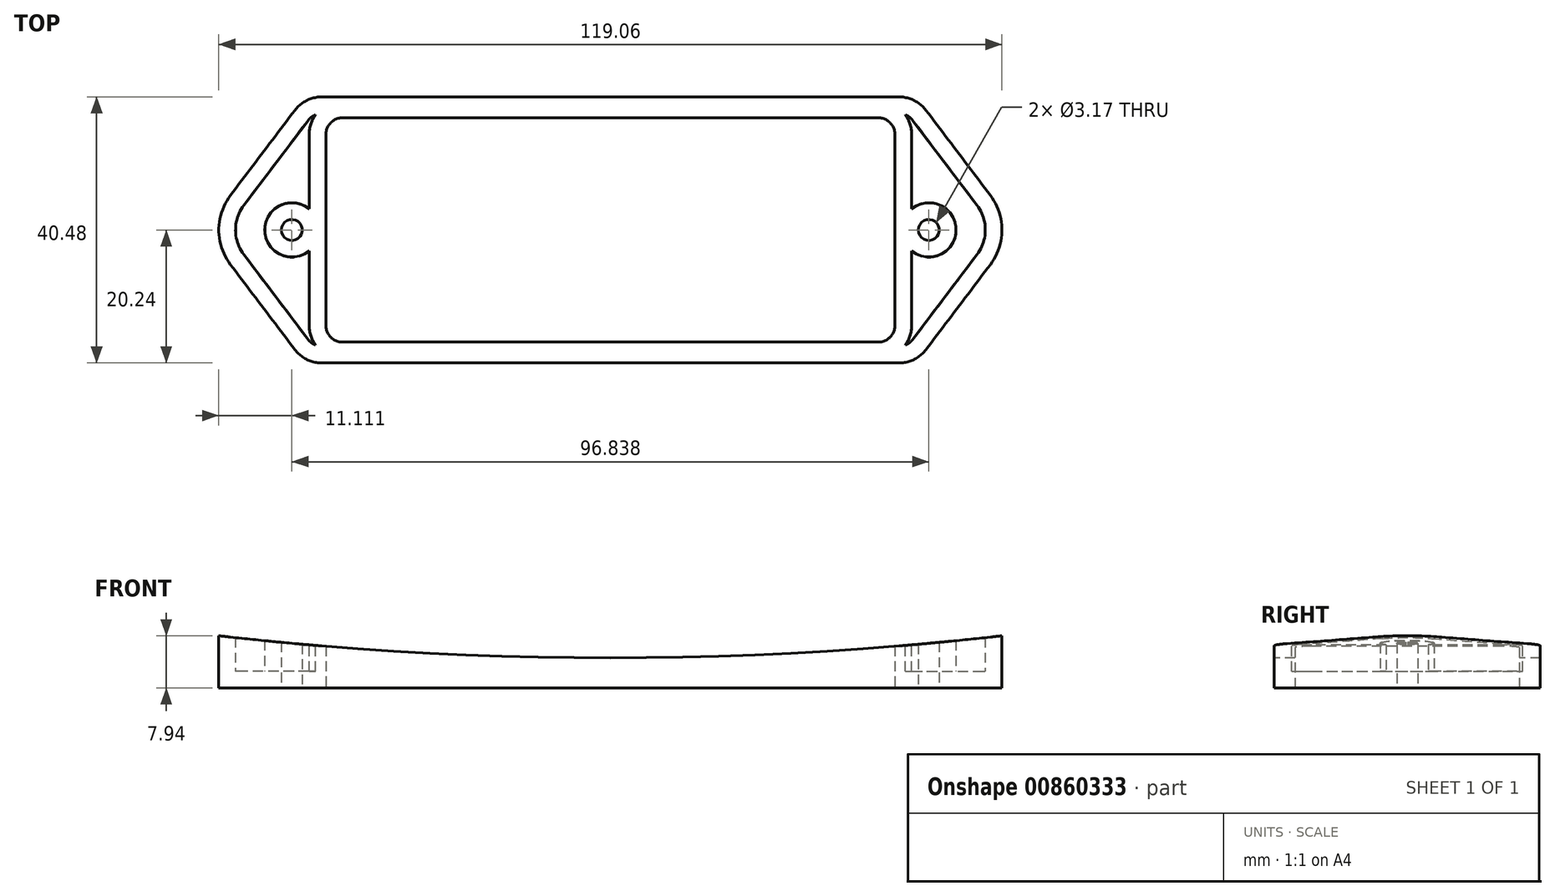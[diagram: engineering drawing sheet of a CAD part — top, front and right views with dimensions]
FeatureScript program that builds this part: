
annotation { "Feature Type Name" : "Feature", "Feature Type Description" : "" }
export const myFeature = defineFeature(function(context is Context, id is Id, definition is map)
    precondition{}
    {
        {
            var Q0;
            Q0=qCreatedBy(makeId("Top.planeOp"),FACE);
            var sketch = newSketch(context, id + "F0", { "sketchPlane" : qUnion([Q0])});
            skLineSegment(sketch, "E0.bottom", {"start": v(43.26, -17.07) * mm, "end": v(-43.26, -17.07) * mm});
            skLineSegment(sketch, "E0.top", {"start": v(43.26, 17.07) * mm, "end": v(-43.26, 17.07) * mm});
            skLineSegment(sketch, "E0.left", {"start": v(43.26, -17.07) * mm, "end": v(43.26, 17.07) * mm});
            skLineSegment(sketch, "E0.right", {"start": v(-43.26, -17.07) * mm, "end": v(-43.26, 17.07) * mm});
            skPoint(sketch, "E0.middle", {"position": v(0, 0) * mm});
            skLineSegment(sketch, "E1.bottom", {"start": v(46.43, -20.24) * mm, "end": v(-46.43, -20.24) * mm});
            skLineSegment(sketch, "E1.top", {"start": v(46.43, 20.24) * mm, "end": v(-46.43, 20.24) * mm});
            skLineSegment(sketch, "E2", {"start": v(59.53, 27.31) * mm, "end": v(59.53, -36.65) * mm});
            skLineSegment(sketch, "E3.MirrorCS", {"start": v(-59.53, 27.31) * mm, "end": v(-59.53, -36.65) * mm});
            skArc(sketch, "E4", {"start": v(57.76, -5.27) * mm, "mid": v(59.53, 0) * mm, "end": v(57.76, 5.27) * mm});
            skLineSegment(sketch, "E5", {"start": v(46.43, 20.24) * mm, "end": v(57.76, 5.27) * mm});
            skLineSegment(sketch, "E6", {"start": v(46.43, -20.24) * mm, "end": v(57.76, -5.27) * mm});
            skCircle(sketch, "E7", {"center": v(48.42, 0) * mm, "radius": 1.59 * mm});
            skLineSegment(sketch, "E8.MirrorCS", {"start": v(-46.43, 20.24) * mm, "end": v(-57.76, 5.27) * mm});
            skArc(sketch, "E9.MirrorCS", {"start": v(-57.76, -5.27) * mm, "mid": v(-59.53, 0) * mm, "end": v(-57.76, 5.27) * mm});
            skLineSegment(sketch, "E10.MirrorCS", {"start": v(-46.43, -20.24) * mm, "end": v(-57.76, -5.27) * mm});
            skCircle(sketch, "E11.MirrorC", {"center": v(-48.42, 0) * mm, "radius": 1.59 * mm});
            skSolve(sketch);
        }
        {
            var Q0;
            Q0=qSketchRegion(id+"F0",true);
            extrude(context, id + "F1", {"entities" : qUnion([Q0]), "depth" : 11.9 * mm, "offsetDistance" : 25.4 * mm});
        }
        {
            var Q0;
            Q0=makeQuery(id+"F1.opExtrude","SWEPT_EDGE",EDGE,{"disambiguationData":[OSD([sQuery(id+"F0.wireOp",EDGE,"E1.bottom"),sQuery(id+"F0.wireOp",EDGE,"E10.MirrorCS")])]});
            var Q1;
            Q1=makeQuery(id+"F1.opExtrude","SWEPT_EDGE",EDGE,{"disambiguationData":[OSD([sQuery(id+"F0.wireOp",EDGE,"E1.bottom"),sQuery(id+"F0.wireOp",EDGE,"E6")])]});
            var Q2;
            Q2=makeQuery(id+"F1.opExtrude","SWEPT_EDGE",EDGE,{"disambiguationData":[OSD([sQuery(id+"F0.wireOp",EDGE,"E1.top"),sQuery(id+"F0.wireOp",EDGE,"E5")])]});
            var Q3;
            Q3=makeQuery(id+"F1.opExtrude","SWEPT_EDGE",EDGE,{"disambiguationData":[OSD([sQuery(id+"F0.wireOp",EDGE,"E1.top"),sQuery(id+"F0.wireOp",EDGE,"E8.MirrorCS")])]});
            fillet(context, id + "F2", {"entities" : qUnion([Q0, Q1, Q2, Q3]), "radius" : 5.08 * mm, "tangentPropagation" : true, "allowEdgeOverflow" : false});
        }
        {
            var Q0;
            Q0=makeQuery(id+"F1.opExtrude","SWEPT_EDGE",EDGE,{"disambiguationData":[OSD([sQuery(id+"F0.wireOp",EDGE,"E0.bottom"),sQuery(id+"F0.wireOp",EDGE,"E0.left")])]});
            var Q1;
            Q1=makeQuery(id+"F1.opExtrude","SWEPT_EDGE",EDGE,{"disambiguationData":[OSD([sQuery(id+"F0.wireOp",EDGE,"E0.top"),sQuery(id+"F0.wireOp",EDGE,"E0.left")])]});
            var Q2;
            Q2=makeQuery(id+"F1.opExtrude","SWEPT_EDGE",EDGE,{"disambiguationData":[OSD([sQuery(id+"F0.wireOp",EDGE,"E0.top"),sQuery(id+"F0.wireOp",EDGE,"E0.right")])]});
            var Q3;
            Q3=makeQuery(id+"F1.opExtrude","SWEPT_EDGE",EDGE,{"disambiguationData":[OSD([sQuery(id+"F0.wireOp",EDGE,"E0.bottom"),sQuery(id+"F0.wireOp",EDGE,"E0.right")])]});
            fillet(context, id + "F3", {"entities" : qUnion([Q0, Q1, Q2, Q3]), "radius" : 2.54 * mm, "tangentPropagation" : true, "allowEdgeOverflow" : false});
        }
        {
            var Q0;
            Q0=makeQuery(id+"F1.opExtrude","SWEPT_FACE",FACE,{"disambiguationData":[OSD([sQuery(id+"F0.wireOp",EDGE,"E1.bottom")])]});
            var sketch = newSketch(context, id + "F4", { "sketchPlane" : qUnion([Q0])});
            skLineSegment(sketch, "E12", {"start": v(-59.53, 0) * mm, "end": v(-59.53, 7.94) * mm, "construction": true});
            skLineSegment(sketch, "E13", {"start": v(59.53, 7.94) * mm, "end": v(59.53, 0) * mm, "construction": true});
            skLineSegment(sketch, "E14", {"start": v(-5.82, 4.57) * mm, "end": v(10.2, 4.57) * mm, "construction": true});
            skArc(sketch, "E15", {"start": v(-59.53, 7.94) * mm, "mid": v(0, 4.57) * mm, "end": v(59.53, 7.94) * mm});
            skPoint(sketch, "E15.third.point", {"position": v(0, 4.57) * mm});
            skLineSegment(sketch, "E16", {"start": v(-59.53, 7.94) * mm, "end": v(-59.53, 20.75) * mm});
            skLineSegment(sketch, "E17", {"start": v(-59.53, 20.75) * mm, "end": v(59.53, 20.75) * mm});
            skLineSegment(sketch, "E18", {"start": v(59.53, 20.75) * mm, "end": v(59.53, 7.94) * mm});
            skSolve(sketch);
        }
        {
            var Q0;
            Q0=qSketchRegion(id+"F4",true);
            extrude(context, id + "F5", {"entities" : qUnion([Q0]), "operationType" : NewBodyOperationType.REMOVE, "endBound" : BoundingType.THROUGH_ALL, "oppositeDirection" : true, "depth" : 25.4 * mm, "offsetDistance" : 25.4 * mm});
        }
        {
            var Q0;
            Q0=makeQuery(id+"F5.boolean.opBoolean","COPY",FACE,{"derivedFrom":makeQuery(id+"F5.opExtrude","SWEPT_FACE",FACE,{"disambiguationData":[OSD([sQuery(id+"F4.wireOp",EDGE,"E15")])]})});
            shell(context, id + "F6", {"entities" : qUnion([Q0]), "thickness" : 2.54 * mm});
        }
    });
